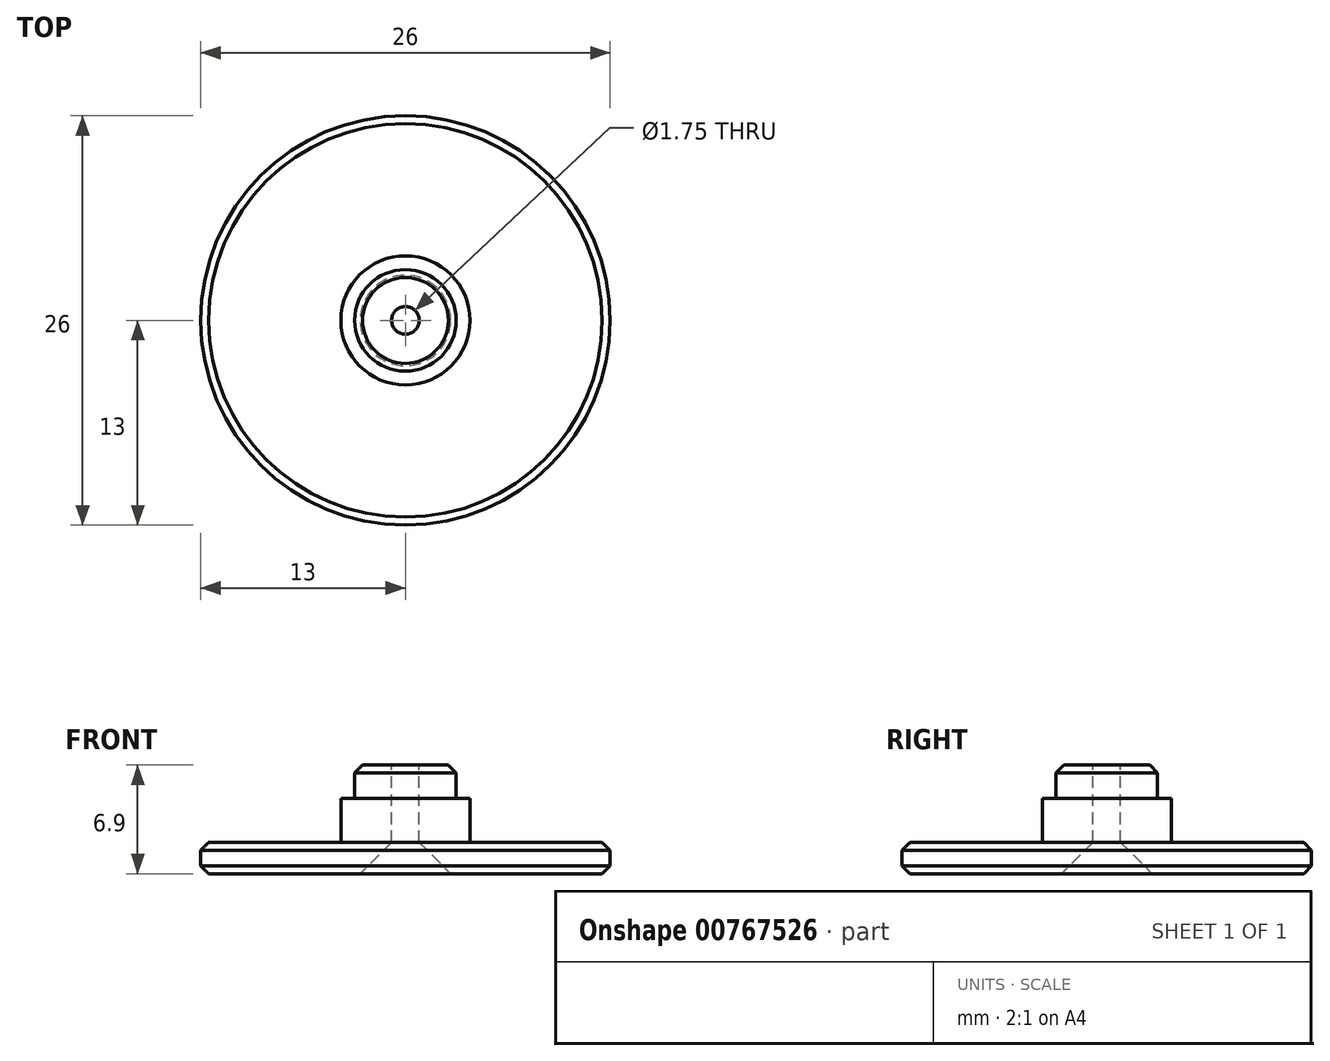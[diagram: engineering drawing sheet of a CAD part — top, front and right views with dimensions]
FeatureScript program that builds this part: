
annotation { "Feature Type Name" : "Feature", "Feature Type Description" : "" }
export const myFeature = defineFeature(function(context is Context, id is Id, definition is map)
    precondition{}
    {
        {
            var Q0;
            Q0=qCreatedBy(makeId("Front.planeOp"),FACE);
            var sketch = newSketch(context, id + "F0", { "sketchPlane" : qUnion([Q0])});
            skLineSegment(sketch, "E0.bottom", {"start": v(0, 0) * mm, "end": v(13, 0) * mm});
            skLineSegment(sketch, "E0.top", {"start": v(0, 1) * mm, "end": v(13, 1) * mm});
            skLineSegment(sketch, "E0.left", {"start": v(0, 0) * mm, "end": v(0, 1) * mm});
            skLineSegment(sketch, "E0.right", {"start": v(13, 0) * mm, "end": v(13, 1) * mm});
            skLineSegment(sketch, "E1", {"start": v(0, 0) * mm, "end": v(0, 3.42) * mm});
            skSolve(sketch);
        }
        {
            var Q0;
            Q0=makeQuery(id+"F0.imprint","IMPRINT",FACE,{"disambiguationData":[TD([[makeQuery(id+"F0.imprint","IMPRINT",EDGE,{"derivedFrom":sQuery(id+"F0.wireOp",EDGE,"E0.bottom")}),1.0]])]});
            var Q1;
            Q1=sQuery(id+"F0.wireOp",EDGE,"E1");
            revolve(context, id + "F1", {"surfaceOperationType" : NewSurfaceOperationType.NEW, "entities" : qUnion([Q0]), "axis" : qUnion([Q1]), "revolveType" : RevolveType.FULL});
        }
        {
            var Q0;
            Q0=makeQuery(id+"F1.opRevolve","SWEPT_FACE",FACE,{"disambiguationData":[OSD([sQuery(id+"F0.wireOp",EDGE,"E0.top")])]});
            var sketch = newSketch(context, id + "F2", { "sketchPlane" : qUnion([Q0])});
            skCircle(sketch, "E2.0", {"center": v(0, 0) * mm, "radius": 8.88 * mm});
            skCircle(sketch, "E3", {"center": v(0, 0) * mm, "radius": 4.1 * mm});
            skSolve(sketch);
        }
        {
            var Q0;
            Q0=makeQuery(id+"F2.imprint","IMPRINT",FACE,{"disambiguationData":[TD([[makeQuery(id+"F2.imprint","IMPRINT",EDGE,{"derivedFrom":sQuery(id+"F2.wireOp",EDGE,"E3")}),1.0]])]});
            extrude(context, id + "F3", {"entities" : qUnion([Q0]), "operationType" : NewBodyOperationType.ADD, "depth" : 2.8 * mm, "offsetDistance" : 25 * mm});
        }
        {
            var Q0;
            Q0=makeQuery(id+"F3.opExtrude","CAP_FACE",FACE,{"disambiguationData":[OSD([sQuery(id+"F2.wireOp",EDGE,"E3")])],"isStart":false});
            var sketch = newSketch(context, id + "F4", { "sketchPlane" : qUnion([Q0])});
            skCircle(sketch, "E4", {"center": v(0, 0) * mm, "radius": 3.22 * mm});
            skSolve(sketch);
        }
        {
            var Q0;
            Q0=makeQuery(id+"F4.imprint","IMPRINT",FACE,{"disambiguationData":[TD([[makeQuery(id+"F4.imprint","IMPRINT",EDGE,{"derivedFrom":sQuery(id+"F4.wireOp",EDGE,"E4")}),1.0]])]});
            extrude(context, id + "F5", {"entities" : qUnion([Q0]), "operationType" : NewBodyOperationType.ADD, "depth" : 2.1 * mm, "offsetDistance" : 25 * mm});
        }
        {
            var Q0;
            Q0=makeQuery(id+"F5.opExtrude","CAP_FACE",FACE,{"disambiguationData":[OSD([sQuery(id+"F4.wireOp",EDGE,"E4")])],"isStart":false});
            var sketch = newSketch(context, id + "F6", { "sketchPlane" : qUnion([Q0])});
            skCircle(sketch, "E5", {"center": v(0, 0) * mm, "radius": 0.88 * mm});
            skSolve(sketch);
        }
        {
            var Q0;
            Q0=makeQuery(id+"F6.imprint","IMPRINT",FACE,{"disambiguationData":[TD([[makeQuery(id+"F6.imprint","IMPRINT",EDGE,{"derivedFrom":sQuery(id+"F6.wireOp",EDGE,"E5")}),1.0]])]});
            extrude(context, id + "F7", {"entities" : qUnion([Q0]), "operationType" : NewBodyOperationType.REMOVE, "endBound" : BoundingType.THROUGH_ALL, "oppositeDirection" : true, "depth" : 25 * mm, "offsetDistance" : 25 * mm});
        }
        {
            var Q0;
            Q0=makeQuery(id+"F1.opRevolve","SWEPT_FACE",FACE,{"disambiguationData":[OSD([sQuery(id+"F0.wireOp",EDGE,"E0.bottom")])]});
            extrude(context, id + "F8", {"entities" : qUnion([Q0]), "operationType" : NewBodyOperationType.ADD, "depth" : 1 * mm, "offsetDistance" : 25 * mm});
        }
        {
            var Q0;
            Q0=makeQuery(id+"F8.opExtrude","CAP_EDGE",EDGE,{"disambiguationData":[OSD([sQuery(id+"F0.wireOp",EDGE,"E0.bottom"),sQuery(id+"F0.wireOp",EDGE,"E0.right")])],"isStart":false});
            var Q1;
            Q1=makeQuery(id+"F1.opRevolve","SWEPT_EDGE",EDGE,{"disambiguationData":[OSD([sQuery(id+"F0.wireOp",EDGE,"E0.top"),sQuery(id+"F0.wireOp",EDGE,"E0.right")])]});
            var Q2;
            Q2=makeQuery(id+"F5.opExtrude","CAP_EDGE",EDGE,{"disambiguationData":[OSD([sQuery(id+"F4.wireOp",EDGE,"E4")])],"isStart":false});
            chamfer(context, id + "F9", {"entities" : qUnion([Q0, Q1, Q2]), "width" : 0.5 * mm, "tangentPropagation" : true});
        }
        {
            var Q0;
            Q0=makeQuery(id+"F8.opExtrude","CAP_EDGE",EDGE,{"disambiguationData":[OSD([sQuery(id+"F0.wireOp",EDGE,"E0.bottom"),sQuery(id+"F6.wireOp",EDGE,"E5")])],"isStart":false});
            chamfer(context, id + "F10", {"entities" : qUnion([Q0]), "width" : 2 * mm, "tangentPropagation" : true});
        }
    });
